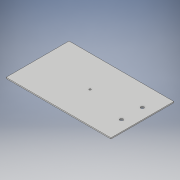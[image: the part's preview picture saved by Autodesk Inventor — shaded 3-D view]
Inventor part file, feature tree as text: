
AUTODESK INVENTOR PART (.ipt)
format: ipt  version: 2019 (Build 230136000, 136)  size: 100,352 bytes
history: native  units: mm
features: extrude x2, sketch x2
ambient origin geometry x8: Origin, YZ Plane, XZ Plane, XY Plane, X Axis, Y Axis, Z Axis, Center Point
bodies: Solid1 (feature_tree)
feature tree (4):
  extrude  "Extrusion1"  Depth=60.0mm
  extrude  "Extrusion2"  Depth=1.0mm
  sketch  "Sketch1"  dims[d0=100.0mm d1=60.0mm]
  sketch  "Sketch2"  dims[d2=1.0mm d3=0.0mm d4=3.0mm d5=3.0mm d6=1.675mm d7=1.0mm d8=0.0mm]
